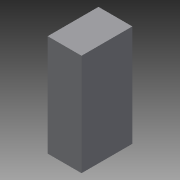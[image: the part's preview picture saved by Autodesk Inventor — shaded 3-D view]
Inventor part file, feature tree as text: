
AUTODESK INVENTOR PART (.ipt)
format: ipt  version: 2014 (Build 180170000, 170)  size: 83,456 bytes
history: native  units: in
note: dims shown in document units (in); Inventor stores cm internally (conversion verified against a paired STEP export)
features: extrude x1, sketch x1
ambient origin geometry x8: Origin, YZ Plane, XZ Plane, XY Plane, X Axis, Y Axis, Z Axis, Center Point
bodies: Solid1 (feature_tree)
feature tree (2):
  extrude  "Extrusion1"  Depth=36.0in
  sketch  "Sketch1"  dims[d0=24.0in d1=36.0in d2=72.0in d3=0.0in]
